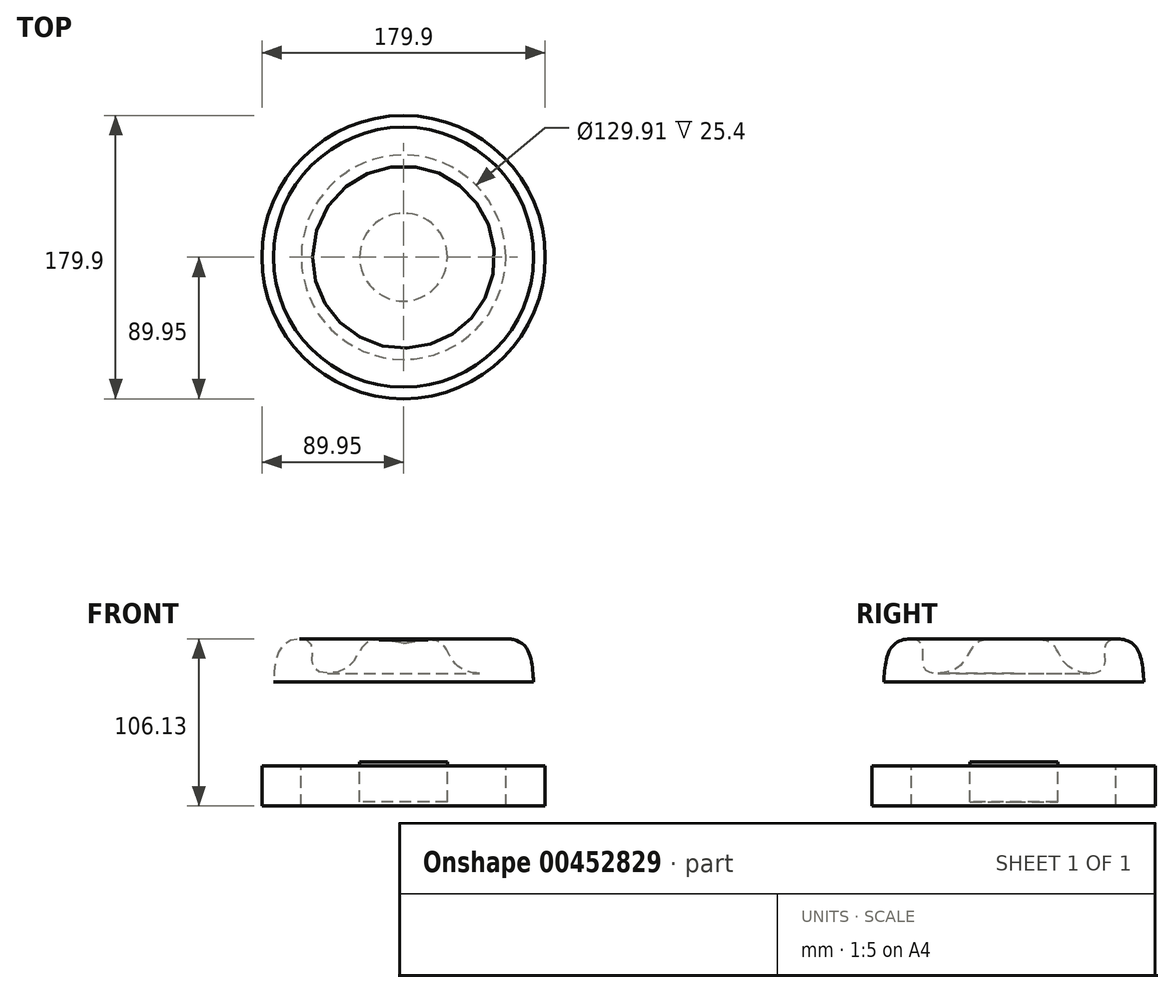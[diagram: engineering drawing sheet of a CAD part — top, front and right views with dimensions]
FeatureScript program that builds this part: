
annotation { "Feature Type Name" : "Feature", "Feature Type Description" : "" }
export const myFeature = defineFeature(function(context is Context, id is Id, definition is map)
    precondition{}
    {
        {
            var Q0;
            Q0=qCreatedBy(makeId("Front.planeOp"),FACE);
            var sketch = newSketch(context, id + "F0", { "sketchPlane" : qUnion([Q0])});
            skLineSegment(sketch, "E0", {"start": v(0, 0) * mm, "end": v(0, 24.56) * mm});
            skFitSpline(sketch, "E1", {"points": [v(0, 24.56) * mm, v(-23.94, 24.56) * mm, v(-35.24, 9.46) * mm, v(-56.76, 8.63) * mm, v(-58.91, 24.56) * mm, v(-75.05, 24.56) * mm, v(-82.59, 0) * mm], "startDerivative": vector(-156.38, 30.21) * mm, "endDerivative": vector(-9.85, -159.32) * mm});
            skLineSegment(sketch, "E2", {"start": v(-82.59, 0) * mm, "end": v(0, 0) * mm});
            skSolve(sketch);
        }
        {
            var Q0;
            Q0 = qSketchRegion(id + "F0", true);
            var Q1;
            Q1=sQuery(id+"F0.wireOp",EDGE,"E0");
            revolve(context, id + "F1", {"entities" : qUnion([Q0]), "axis" : qUnion([Q1]), "revolveType" : RevolveType.FULL});
        }
        {
            var Q0;
            Q0=qCreatedBy(makeId("Top.planeOp"),FACE);
            cPlane(context, id + "F2", {"entities" : qUnion([Q0]), "cplaneType" : CPlaneType.OFFSET, "offset" : 50.8 * mm, "oppositeDirection" : true, "width" : 152.4 * mm, "height" : 152.4 * mm});
        }
        {
            var Q0;
            Q0=qCreatedBy(id+"F2.planeOp",FACE);
            var sketch = newSketch(context, id + "F3", { "sketchPlane" : qUnion([Q0])});
            skCircle(sketch, "E3", {"center": v(0, 0) * mm, "radius": 79.93 * mm});
            skCircle(sketch, "E4", {"center": v(0, 0) * mm, "radius": 27.89 * mm});
            skCircle(sketch, "E5", {"center": v(0, 0) * mm, "radius": 53.72 * mm});
            skSolve(sketch);
        }
        {
            var Q0;
            Q0=makeQuery(id+"F3.imprint","IMPRINT",FACE,{"disambiguationData":[TD([[makeQuery(id+"F3.imprint","IMPRINT",EDGE,{"derivedFrom":sQuery(id+"F3.wireOp",EDGE,"E4")}),1.0]])]});
            extrude(context, id + "F4", {"entities" : qUnion([Q0]), "oppositeDirection" : true, "depth" : 25.4 * mm, "offsetDistance" : 25.4 * mm});
        }
        {
            var Q0;
            Q0=qCreatedBy(makeId("Top.planeOp"),FACE);
            cPlane(context, id + "F5", {"entities" : qUnion([Q0]), "cplaneType" : CPlaneType.OFFSET, "offset" : 53.34 * mm, "oppositeDirection" : true, "width" : 152.4 * mm, "height" : 152.4 * mm});
        }
        {
            var Q0;
            Q0=qCreatedBy(id+"F5.planeOp",FACE);
            var sketch = newSketch(context, id + "F6", { "sketchPlane" : qUnion([Q0])});
            skCircle(sketch, "E6", {"center": v(0, 0) * mm, "radius": 64.96 * mm});
            skCircle(sketch, "E7", {"center": v(0, 0) * mm, "radius": 89.95 * mm});
            skSolve(sketch);
        }
        {
            var Q0;
            Q0=makeQuery(id+"F6.imprint","IMPRINT",FACE,{"disambiguationData":[TD([[makeQuery(id+"F6.imprint","IMPRINT",EDGE,{"derivedFrom":sQuery(id+"F6.wireOp",EDGE,"E6")}),-1.0]])]});
            extrude(context, id + "F7", {"entities" : qUnion([Q0]), "oppositeDirection" : true, "depth" : 25.4 * mm, "offsetDistance" : 25.4 * mm});
        }
        {
            var Q0;
            Q0=qCreatedBy(makeId("Right.planeOp"),FACE);
            var sketch = newSketch(context, id + "F8", { "sketchPlane" : qUnion([Q0])});
            skLineSegment(sketch, "E8", {"start": v(-0.13, 24.24) * mm, "end": v(-0.13, -72.53) * mm});
            skSolve(sketch);
        }
        {
            var Q0;
            Q0=sQuery(id+"F8.wireOp",EDGE,"E8");
            cPlane(context, id + "F9", {"entities" : qUnion([Q0]), "cplaneType" : CPlaneType.LINE_ANGLE, "offset" : 25.4 * mm, "angle" : 30 * degree, "oppositeDirection" : true, "width" : 152.4 * mm, "height" : 152.4 * mm});
        }
        {
            var Q0;
            Q0=qCreatedBy(id+"F9.planeOp",FACE);
            var Q1;
            Q1=sQuery(id+"F8.wireOp",EDGE,"E8");
            cPlane(context, id + "F10", {"entities" : qUnion([Q0, Q1]), "cplaneType" : CPlaneType.LINE_ANGLE, "offset" : 25.4 * mm, "angle" : 30 * degree, "oppositeDirection" : true, "width" : 152.4 * mm, "height" : 152.4 * mm});
        }
    });
